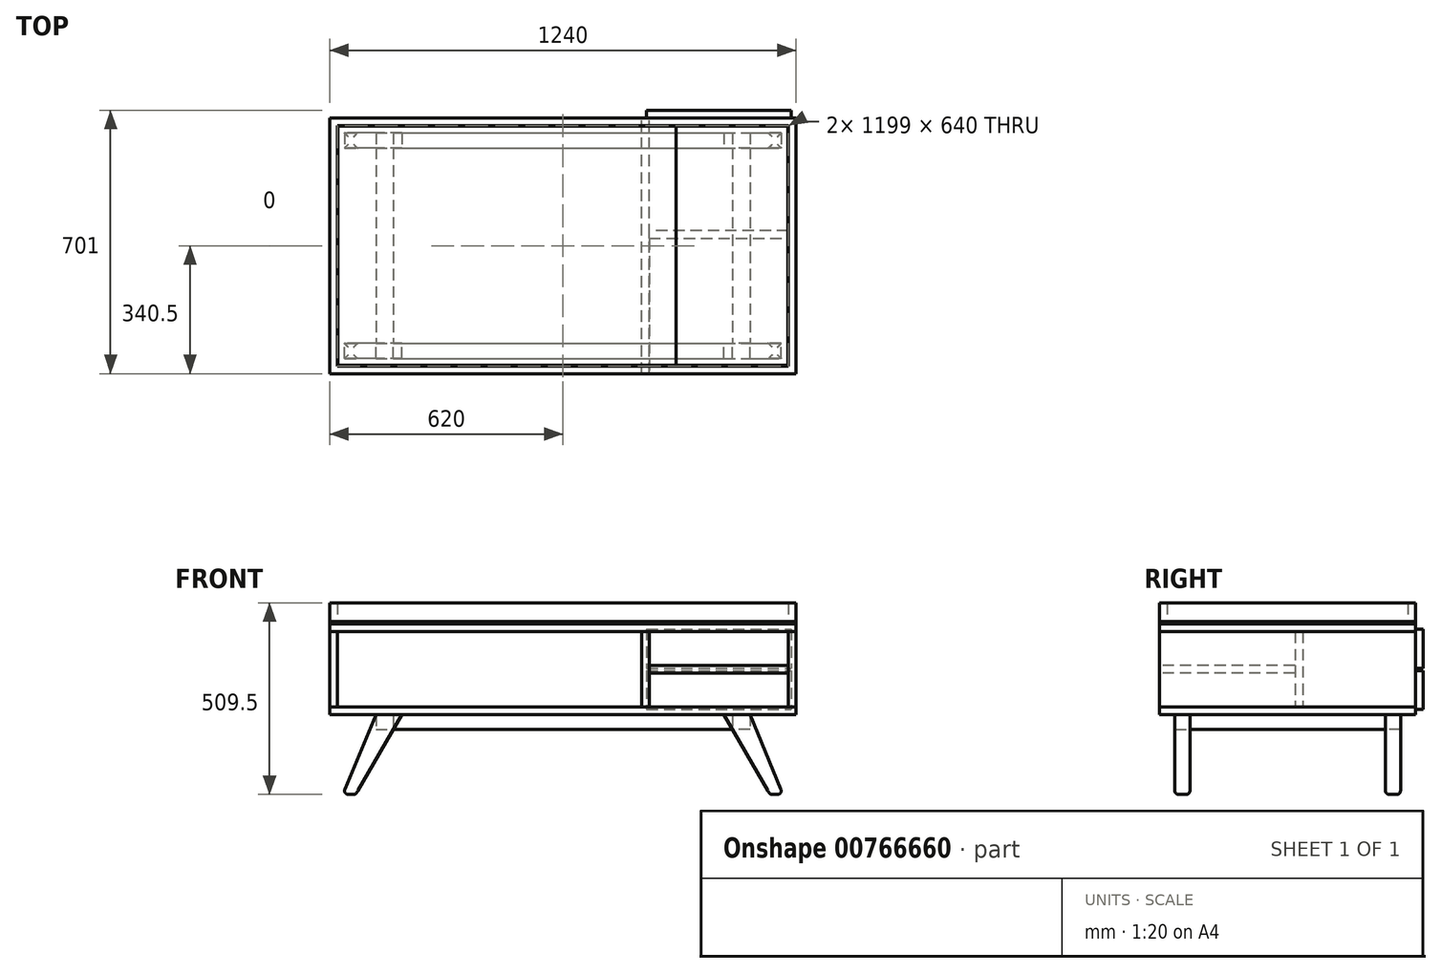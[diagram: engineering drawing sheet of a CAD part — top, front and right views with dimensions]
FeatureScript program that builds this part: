
annotation { "Feature Type Name" : "Feature", "Feature Type Description" : "" }
export const myFeature = defineFeature(function(context is Context, id is Id, definition is map)
    precondition{}
    {
        {
            var Q0;
            Q0=qCreatedBy(makeId("Front.planeOp"),FACE);
            var sketch = newSketch(context, id + "F0", { "sketchPlane" : qUnion([Q0])});
            skLineSegment(sketch, "E0.bottom", {"start": v(-620, 0) * mm, "end": v(620, 0) * mm});
            skLineSegment(sketch, "E0.top", {"start": v(-620, -241) * mm, "end": v(620, -241) * mm});
            skLineSegment(sketch, "E1", {"start": v(229.5, -20.5) * mm, "end": v(229.5, -220.5) * mm});
            skLineSegment(sketch, "E2.0", {"start": v(-620, -20.5) * mm, "end": v(620, -20.5) * mm});
            skLineSegment(sketch, "E2.2", {"start": v(-620, -220.5) * mm, "end": v(620, -220.5) * mm});
            skLineSegment(sketch, "E3.trimOffspring", {"start": v(-599.5, -20.5) * mm, "end": v(-599.5, -220.5) * mm});
            skLineSegment(sketch, "E4.trimOffspring", {"start": v(599.5, -20.5) * mm, "end": v(599.5, -220.5) * mm});
            skLineSegment(sketch, "E5.trimOffspring", {"start": v(-620, 0) * mm, "end": v(-620, -241) * mm});
            skLineSegment(sketch, "E6.trimOffspring", {"start": v(620, 0) * mm, "end": v(620, -241) * mm});
            skLineSegment(sketch, "E7", {"start": v(229.5, -120.5) * mm, "end": v(599.5, -120.5) * mm, "construction": true});
            skLineSegment(sketch, "E8", {"start": v(229.5, -110.25) * mm, "end": v(599.5, -110.25) * mm});
            skLineSegment(sketch, "E9", {"start": v(229.5, -130.75) * mm, "end": v(599.5, -130.75) * mm});
            skLineSegment(sketch, "E10.0", {"start": v(209, -20.5) * mm, "end": v(209, -220.5) * mm});
            skPoint(sketch, "E11", {"position": v(0, 0) * mm});
            skSolve(sketch);
        }
        {
            var Q0;
            {var subQ1=sQuery(id+"F0.wireOp",EDGE,"E0.top");Q0=makeQuery(id+"F0.imprint","IMPRINT",FACE,{"disambiguationData":[TD([[makeQuery(id+"F0.imprint","IMPRINT",EDGE,{"derivedFrom":subQ1}),1.0]])]});}
            extrude(context, id + "F1", {"entities" : qUnion([Q0]), "depth" : 681 / 2 * mm, "offsetDistance" : 25 * mm, "hasSecondDirection" : true, "secondDirectionOppositeDirection" : true, "secondDirectionDepth" : 681 / 2 * mm});
        }
        {
            var Q0;
            {var subQ0=sQuery(id+"F0.wireOp",EDGE,"60a11fd1-bdb7-46c1-8277-bfbef1fc92c4.0");Q0=makeQuery(id+"F0.imprint","IMPRINT",FACE,{"disambiguationData":[TD([[makeQuery(id+"F0.imprint","IMPRINT",EDGE,{"derivedFrom":subQ0}),-1.0]])]});}
            var Q1;
            {var subQ0=sQuery(id+"F0.wireOp",EDGE,"E1");Q1=makeQuery(id+"F0.imprint","IMPRINT",FACE,{"disambiguationData":[TD([[makeQuery(id+"F0.imprint","IMPRINT",EDGE,{"derivedFrom":subQ0}),-1.0]])]});}
            var Q2;
            {var subQ3=sQuery(id+"F0.wireOp",EDGE,"60a11fd1-bdb7-46c1-8277-bfbef1fc92c4.2");Q2=makeQuery(id+"F0.imprint","IMPRINT",FACE,{"disambiguationData":[TD([[makeQuery(id+"F0.imprint","IMPRINT",EDGE,{"derivedFrom":subQ3}),1.0]])]});}
            var Q3;
            {var subQ2=sQuery(id+"F0.wireOp",EDGE,"E2.2");var subQ4=sQuery(id+"F0.wireOp",EDGE,"E0.left");var subQ5=makeQuery(id+"F0.imprint","INTERSECT",VERTEX,{"derivedFrom":[subQ4,subQ2]});Q3=makeQuery(id+"F0.imprint","IMPRINT",FACE,{"disambiguationData":[TD([[makeQuery(id+"F0.imprint","IMPRINT",EDGE,{"disambiguationData":[TD([[subQ5,1.0]])],"derivedFrom":subQ4}),1.0]])]});}
            var Q4;
            {var subQ3=sQuery(id+"F0.wireOp",EDGE,"E3.trimOffspring");Q4=makeQuery(id+"F0.imprint","IMPRINT",FACE,{"disambiguationData":[TD([[makeQuery(id+"F0.imprint","IMPRINT",EDGE,{"derivedFrom":subQ3}),-1.0]])]});}
            var Q5;
            {var subQ3=sQuery(id+"F0.wireOp",EDGE,"E4.trimOffspring");Q5=makeQuery(id+"F0.imprint","IMPRINT",FACE,{"disambiguationData":[TD([[makeQuery(id+"F0.imprint","IMPRINT",EDGE,{"derivedFrom":subQ3}),1.0]])]});}
            var Q6;
            Q6=makeQuery(id+"F1.opExtrude","CAP_FACE",FACE,{"disambiguationData":[OSD([sQuery(id+"F0.wireOp",EDGE,"E0.top"),sQuery(id+"F0.wireOp",EDGE,"E0.left"),sQuery(id+"F0.wireOp",EDGE,"E0.right"),sQuery(id+"F0.wireOp",EDGE,"E2.2")])],"isStart":false});
            var Q7;
            Q7=makeQuery(id+"F1.opExtrude","CAP_FACE",FACE,{"disambiguationData":[OSD([sQuery(id+"F0.wireOp",EDGE,"E0.top"),sQuery(id+"F0.wireOp",EDGE,"E0.left"),sQuery(id+"F0.wireOp",EDGE,"E0.right"),sQuery(id+"F0.wireOp",EDGE,"E2.2")])],"isStart":true});
            extrude(context, id + "F2", {"entities" : qUnion([Q0, Q1, Q2, Q3, Q4, Q5]), "endBound" : BoundingType.UP_TO_SURFACE, "depth" : 25 * mm, "endBoundEntityFace" : qUnion([Q6]), "offsetDistance" : 25 * mm, "hasSecondDirection" : true, "secondDirectionBound" : SecondDirectionBoundingType.UP_TO_SURFACE, "secondDirectionOppositeDirection" : true, "secondDirectionDepth" : 25 * mm, "secondDirectionBoundEntityFace" : qUnion([Q7])});
        }
        {
            var Q0;
            {var subQ6=sQuery(id+"F0.wireOp",EDGE,"E0.bottom");Q0=makeQuery(id+"F0.imprint","IMPRINT",FACE,{"disambiguationData":[TD([[makeQuery(id+"F0.imprint","IMPRINT",EDGE,{"derivedFrom":subQ6}),-1.0]])]});}
            var Q1;
            Q1=makeQuery(id+"F1.opExtrude","CAP_FACE",FACE,{"disambiguationData":[OSD([sQuery(id+"F0.wireOp",EDGE,"E0.top"),sQuery(id+"F0.wireOp",EDGE,"E0.left"),sQuery(id+"F0.wireOp",EDGE,"E0.right"),sQuery(id+"F0.wireOp",EDGE,"E2.2")])],"isStart":false});
            var Q2;
            Q2=makeQuery(id+"F1.opExtrude","CAP_FACE",FACE,{"disambiguationData":[OSD([sQuery(id+"F0.wireOp",EDGE,"E0.top"),sQuery(id+"F0.wireOp",EDGE,"E0.left"),sQuery(id+"F0.wireOp",EDGE,"E0.right"),sQuery(id+"F0.wireOp",EDGE,"E2.2")])],"isStart":true});
            extrude(context, id + "F3", {"entities" : qUnion([Q0]), "endBound" : BoundingType.UP_TO_SURFACE, "depth" : 25 * mm, "endBoundEntityFace" : qUnion([Q1]), "offsetDistance" : 25 * mm, "hasSecondDirection" : true, "secondDirectionBound" : SecondDirectionBoundingType.UP_TO_SURFACE, "secondDirectionOppositeDirection" : true, "secondDirectionDepth" : 25 * mm, "secondDirectionBoundEntityFace" : qUnion([Q2])});
        }
        {
            var Q0;
            Q0=qCreatedBy(makeId("Front.planeOp"),FACE);
            cPlane(context, id + "F4", {"entities" : qUnion([Q0]), "cplaneType" : CPlaneType.OFFSET, "offset" : 260 * mm, "width" : 150 * mm, "height" : 150 * mm});
        }
        {
            var Q0;
            Q0=qCreatedBy(id+"F4.planeOp",FACE);
            var sketch = newSketch(context, id + "F5", { "sketchPlane" : qUnion([Q0])});
            skLineSegment(sketch, "E12", {"start": v(-620, -62.26) * mm, "end": v(-620, -556.12) * mm, "construction": true});
            skLineSegment(sketch, "E13", {"start": v(620, -20.15) * mm, "end": v(620, -556.12) * mm, "construction": true});
            skLineSegment(sketch, "E14", {"start": v(-1066.77, -241) * mm, "end": v(893.35, -241) * mm});
            skLineSegment(sketch, "E15", {"start": v(-497.31, -241) * mm, "end": v(-620, -453.5) * mm});
            skLineSegment(sketch, "E16", {"start": v(-620, -453.5) * mm, "end": v(-550.72, -453.5) * mm});
            skLineSegment(sketch, "E17", {"start": v(-428.03, -241) * mm, "end": v(-550.72, -453.5) * mm});
            skLineSegment(sketch, "E18.MirrorCS", {"start": v(620, -453.5) * mm, "end": v(550.72, -453.5) * mm});
            skLineSegment(sketch, "E19.MirrorCS", {"start": v(497.31, -241) * mm, "end": v(620, -453.5) * mm});
            skLineSegment(sketch, "E20.MirrorCS", {"start": v(428.03, -241) * mm, "end": v(550.72, -453.5) * mm});
            skLineSegment(sketch, "E21", {"start": v(-451.13, -281) * mm, "end": v(451.13, -281) * mm});
            skLineSegment(sketch, "E22", {"start": v(-497.31, -241) * mm, "end": v(-585.36, -453.5) * mm});
            skLineSegment(sketch, "E23", {"start": v(497.31, -241) * mm, "end": v(585.36, -453.5) * mm});
            skSolve(sketch);
        }
        {
            var Q0;
            {var subQ4=sQuery(id+"F5.wireOp",EDGE,"E22");Q0=makeQuery(id+"F5.imprint","IMPRINT",FACE,{"disambiguationData":[TD([[makeQuery(id+"F5.imprint","IMPRINT",EDGE,{"derivedFrom":subQ4}),1.0]])]});}
            var Q1;
            {var subQ4=sQuery(id+"F5.wireOp",EDGE,"E23");Q1=makeQuery(id+"F5.imprint","IMPRINT",FACE,{"disambiguationData":[TD([[makeQuery(id+"F5.imprint","IMPRINT",EDGE,{"derivedFrom":subQ4}),-1.0]])]});}
            extrude(context, id + "F6", {"entities" : qUnion([Q0, Q1]), "depth" : 40 * mm, "offsetDistance" : 25 * mm});
        }
        {
            var Q0;
            Q0=makeQuery(id+"F6.opExtrude","CAP_EDGE",EDGE,{"disambiguationData":[OSD([sQuery(id+"F5.wireOp",EDGE,"E16")])],"isStart":false});
            var Q1;
            Q1=makeQuery(id+"F6.opExtrude","SWEPT_EDGE",EDGE,{"disambiguationData":[OSD([sQuery(id+"F5.wireOp",EDGE,"E16"),sQuery(id+"F5.wireOp",EDGE,"E17")])]});
            var Q2;
            Q2=makeQuery(id+"F6.opExtrude","CAP_EDGE",EDGE,{"disambiguationData":[OSD([sQuery(id+"F5.wireOp",EDGE,"E16")])],"isStart":true});
            var Q3;
            Q3=makeQuery(id+"F6.opExtrude","SWEPT_EDGE",EDGE,{"disambiguationData":[OSD([sQuery(id+"F5.wireOp",EDGE,"E15"),sQuery(id+"F5.wireOp",EDGE,"E16")])]});
            var Q4;
            Q4=makeQuery(id+"F6.opExtrude","CAP_EDGE",EDGE,{"disambiguationData":[OSD([sQuery(id+"F5.wireOp",EDGE,"E18.MirrorCS")])],"isStart":false});
            var Q5;
            Q5=makeQuery(id+"F6.opExtrude","SWEPT_EDGE",EDGE,{"disambiguationData":[OSD([sQuery(id+"F5.wireOp",EDGE,"E18.MirrorCS"),sQuery(id+"F5.wireOp",EDGE,"E20.MirrorCS")])]});
            var Q6;
            Q6=makeQuery(id+"F6.opExtrude","CAP_EDGE",EDGE,{"disambiguationData":[OSD([sQuery(id+"F5.wireOp",EDGE,"E18.MirrorCS")])],"isStart":true});
            var Q7;
            Q7=makeQuery(id+"F6.opExtrude","SWEPT_EDGE",EDGE,{"disambiguationData":[OSD([sQuery(id+"F5.wireOp",EDGE,"E18.MirrorCS"),sQuery(id+"F5.wireOp",EDGE,"E19.MirrorCS")])]});
            fillet(context, id + "F7", {"entities" : qUnion([Q0, Q1, Q2, Q3, Q4, Q5, Q6, Q7]), "tangentPropagation" : true, "radius" : 10 * mm, "defaultsChanged" : true, "vertexSettings" : [], "allowEdgeOverflow" : false});
        }
        {
            var Q0;
            {var subQ5=sQuery(id+"F5.wireOp",EDGE,"E21");Q0=makeQuery(id+"F5.imprint","IMPRINT",FACE,{"disambiguationData":[TD([[makeQuery(id+"F5.imprint","IMPRINT",EDGE,{"derivedFrom":subQ5}),1.0]])]});}
            extrude(context, id + "F8", {"entities" : qUnion([Q0]), "depth" : 40 * mm, "offsetDistance" : 25 * mm});
        }
        {
            var Q0;
            Q0=makeQuery(id+"F6.opExtrude","SWEPT_BODY",BODY,{"disambiguationData":[OSD([sQuery(id+"F5.wireOp",EDGE,"E14"),sQuery(id+"F5.wireOp",EDGE,"E15"),sQuery(id+"F5.wireOp",EDGE,"E16"),sQuery(id+"F5.wireOp",EDGE,"E17")])]});
            var Q1;
            Q1=makeQuery(id+"F6.opExtrude","SWEPT_BODY",BODY,{"disambiguationData":[OSD([sQuery(id+"F5.wireOp",EDGE,"E14"),sQuery(id+"F5.wireOp",EDGE,"E18.MirrorCS"),sQuery(id+"F5.wireOp",EDGE,"E19.MirrorCS"),sQuery(id+"F5.wireOp",EDGE,"E20.MirrorCS")])]});
            var Q2;
            Q2=makeQuery(id+"F8.opExtrude","SWEPT_BODY",BODY,{"disambiguationData":[OSD([sQuery(id+"F5.wireOp",EDGE,"E14"),sQuery(id+"F5.wireOp",EDGE,"E17"),sQuery(id+"F5.wireOp",EDGE,"E20.MirrorCS"),sQuery(id+"F5.wireOp",EDGE,"E21")])]});
            var Q3;
            Q3=qCreatedBy(makeId("Front.planeOp"),FACE);
            mirror(context, id + "F9", {"entities" : qUnion([Q0, Q1, Q2]), "mirrorPlane" : qUnion([Q3])});
        }
        {
            var Q0;
            {var subQ5=sQuery(id+"F5.wireOp",EDGE,"E18.MirrorCS");Q0=makeQuery(id+"F5.imprint","IMPRINT",FACE,{"disambiguationData":[TD([[makeQuery(id+"F5.imprint","IMPRINT",EDGE,{"derivedFrom":subQ5}),-1.0]])]});}
            var sketch = newSketch(context, id + "F10", { "sketchPlane" : qUnion([Q0])});
            skPoint(sketch, "E24.0", {"position": v(497.31, -241) * mm});
            skPoint(sketch, "E25.0", {"position": v(451.13, -281) * mm});
            skLineSegment(sketch, "E26.bottom", {"start": v(497.31, -241) * mm, "end": v(451.13, -241) * mm});
            skLineSegment(sketch, "E26.top", {"start": v(497.31, -281) * mm, "end": v(451.13, -281) * mm});
            skLineSegment(sketch, "E26.left", {"start": v(497.31, -241) * mm, "end": v(497.31, -281) * mm});
            skLineSegment(sketch, "E26.right", {"start": v(451.13, -241) * mm, "end": v(451.13, -281) * mm});
            skLineSegment(sketch, "E27.MirrorCS", {"start": v(-497.31, -241) * mm, "end": v(-451.13, -241) * mm});
            skLineSegment(sketch, "E28.MirrorCS", {"start": v(-451.13, -241) * mm, "end": v(-451.13, -281) * mm});
            skLineSegment(sketch, "E29.MirrorCS", {"start": v(-497.31, -241) * mm, "end": v(-497.31, -281) * mm});
            skLineSegment(sketch, "E30.MirrorCS", {"start": v(-497.31, -281) * mm, "end": v(-451.13, -281) * mm});
            skSolve(sketch);
        }
        {
            var Q0;
            Q0=qSketchRegion(id+"F10",true);
            extrude(context, id + "F11", {"entities" : qUnion([Q0]), "endBound" : BoundingType.UP_TO_NEXT, "oppositeDirection" : true, "depth" : 25 * mm, "offsetDistance" : 25 * mm});
        }
        {
            var Q0;
            Q0=makeQuery(id+"F2.opExtrude","CAP_FACE",FACE,{"disambiguationData":[OSD([sQuery(id+"F0.wireOp",EDGE,"E1"),sQuery(id+"F0.wireOp",EDGE,"E2.0"),sQuery(id+"F0.wireOp",EDGE,"E2.2"),sQuery(id+"F0.wireOp",EDGE,"ae8f2980-7300-4422-b546-210f4e41f4ac.trimOffspring"),sQuery(id+"F0.wireOp",EDGE,"E4.trimOffspring"),sQuery(id+"F0.wireOp",EDGE,"E6.trimOffspring"),sQuery(id+"F0.wireOp",EDGE,"E8"),sQuery(id+"F0.wireOp",EDGE,"E9")])],"isStart":true});
            var sketch = newSketch(context, id + "F12", { "sketchPlane" : qUnion([Q0])});
            skPoint(sketch, "E31.orphan", {"position": v(620, -20.5) * mm});
            skPoint(sketch, "E32.orphan", {"position": v(620, -220.5) * mm});
            skLineSegment(sketch, "E33.0", {"start": v(-229.5, -20.5) * mm, "end": v(-599.5, -20.5) * mm, "construction": true});
            skLineSegment(sketch, "E34.0", {"start": v(-599.5, -20.5) * mm, "end": v(-599.5, -110.25) * mm, "construction": true});
            skLineSegment(sketch, "E35.0", {"start": v(-229.5, -220.5) * mm, "end": v(-599.5, -220.5) * mm, "construction": true});
            skLineSegment(sketch, "E36.0", {"start": v(-229.5, -20.5) * mm, "end": v(-229.5, -110.25) * mm, "construction": true});
            skLineSegment(sketch, "E37.0", {"start": v(-229.5, -110.25) * mm, "end": v(-599.5, -110.25) * mm, "construction": true});
            skLineSegment(sketch, "E38.0", {"start": v(-229.5, -130.75) * mm, "end": v(-599.5, -130.75) * mm, "construction": true});
            skLineSegment(sketch, "E39.trimOffspring", {"start": v(-599.5, -130.75) * mm, "end": v(-599.5, -220.5) * mm, "construction": true});
            skLineSegment(sketch, "E40.trimOffspring", {"start": v(-229.5, -130.75) * mm, "end": v(-229.5, -220.5) * mm, "construction": true});
            skPoint(sketch, "E41.orphan", {"position": v(-620, -220.5) * mm});
            skPoint(sketch, "E42.orphan", {"position": v(-620, -20.5) * mm});
            skLineSegment(sketch, "E43.0", {"start": v(-222.5, -13.5) * mm, "end": v(-606.5, -13.5) * mm});
            skLineSegment(sketch, "E43.1", {"start": v(-222.5, -13.5) * mm, "end": v(-222.5, -117.25) * mm});
            skLineSegment(sketch, "E43.2", {"start": v(-222.5, -117.25) * mm, "end": v(-606.5, -117.25) * mm});
            skLineSegment(sketch, "E43.3", {"start": v(-606.5, -13.5) * mm, "end": v(-606.5, -117.25) * mm});
            skLineSegment(sketch, "E44.0", {"start": v(-222.5, -123.75) * mm, "end": v(-606.5, -123.75) * mm});
            skLineSegment(sketch, "E44.1", {"start": v(-222.5, -123.75) * mm, "end": v(-222.5, -227.5) * mm});
            skLineSegment(sketch, "E44.2", {"start": v(-222.5, -227.5) * mm, "end": v(-606.5, -227.5) * mm});
            skLineSegment(sketch, "E44.3", {"start": v(-606.5, -123.75) * mm, "end": v(-606.5, -227.5) * mm});
            skSolve(sketch);
        }
        {
            var Q0;
            {var subQ0=sQuery(id+"F12.wireOp",EDGE,"E43.3");var subQ1=sQuery(id+"F12.wireOp",EDGE,"E43.2");var subQ2=makeQuery(id+"F12.imprint","INTERSECT",VERTEX,{"derivedFrom":[subQ1,subQ0]});Q0=makeQuery(id+"F12.imprint","IMPRINT",FACE,{"disambiguationData":[TD([[makeQuery(id+"F12.imprint","IMPRINT",EDGE,{"disambiguationData":[TD([[subQ2,1.0]])],"derivedFrom":subQ1}),-1.0]])]});}
            var Q1;
            {var subQ1=sQuery(id+"F12.wireOp",EDGE,"E43.0");Q1=makeQuery(id+"F12.imprint","IMPRINT",FACE,{"disambiguationData":[TD([[makeQuery(id+"F12.imprint","IMPRINT",EDGE,{"derivedFrom":subQ1}),1.0]])]});}
            var Q2;
            {var subQ0=sQuery(id+"F12.wireOp",EDGE,"E44.3");var subQ1=sQuery(id+"F12.wireOp",EDGE,"E44.0");var subQ2=makeQuery(id+"F12.imprint","INTERSECT",VERTEX,{"derivedFrom":[subQ1,subQ0]});Q2=makeQuery(id+"F12.imprint","IMPRINT",FACE,{"disambiguationData":[TD([[makeQuery(id+"F12.imprint","IMPRINT",EDGE,{"disambiguationData":[TD([[subQ2,1.0]])],"derivedFrom":subQ1}),1.0]])]});}
            var Q3;
            {var subQ1=sQuery(id+"F12.wireOp",EDGE,"E44.1");Q3=makeQuery(id+"F12.imprint","IMPRINT",FACE,{"disambiguationData":[TD([[makeQuery(id+"F12.imprint","IMPRINT",EDGE,{"derivedFrom":subQ1}),-1.0]])]});}
            extrude(context, id + "F13", {"entities" : qUnion([Q0, Q1, Q2, Q3]), "depth" : 20 * mm, "offsetDistance" : 25 * mm});
        }
        {
            var Q0;
            Q0=makeQuery(id+"F3.opExtrude","SWEPT_FACE",FACE,{"disambiguationData":[OSD([sQuery(id+"F0.wireOp",EDGE,"E0.bottom")])]});
            var sketch = newSketch(context, id + "F14", { "sketchPlane" : qUnion([Q0])});
            skLineSegment(sketch, "E45.0", {"start": v(-620, -340.5) * mm, "end": v(-620, 340.5) * mm});
            skLineSegment(sketch, "E45.1", {"start": v(-620, 340.5) * mm, "end": v(620, 340.5) * mm});
            skLineSegment(sketch, "E45.2", {"start": v(620, -340.5) * mm, "end": v(620, 340.5) * mm});
            skLineSegment(sketch, "E45.3", {"start": v(-620, -340.5) * mm, "end": v(620, -340.5) * mm});
            skLineSegment(sketch, "E46.0", {"start": v(-599.5, 320) * mm, "end": v(-599.5, -320) * mm});
            skLineSegment(sketch, "E46.1", {"start": v(599.5, 320) * mm, "end": v(-599.5, 320) * mm});
            skLineSegment(sketch, "E46.2", {"start": v(599.5, -320) * mm, "end": v(599.5, 320) * mm});
            skLineSegment(sketch, "E46.3", {"start": v(-599.5, -320) * mm, "end": v(599.5, -320) * mm});
            skLineSegment(sketch, "E47.0", {"start": v(-615, 335.5) * mm, "end": v(-615, -335.5) * mm});
            skLineSegment(sketch, "E47.1", {"start": v(615, 335.5) * mm, "end": v(-615, 335.5) * mm});
            skLineSegment(sketch, "E47.2", {"start": v(615, -335.5) * mm, "end": v(615, 335.5) * mm});
            skLineSegment(sketch, "E47.3", {"start": v(-615, -335.5) * mm, "end": v(615, -335.5) * mm});
            skSolve(sketch);
        }
        {
            var Q0;
            Q0=makeQuery(id+"F14.imprint","IMPRINT",FACE,{"disambiguationData":[TD([[makeQuery(id+"F14.imprint","IMPRINT",EDGE,{"derivedFrom":sQuery(id+"F14.wireOp",EDGE,"E46.0")}),-1.0]])]});
            var Q1;
            Q1=makeQuery(id+"F14.imprint","IMPRINT",FACE,{"disambiguationData":[TD([[makeQuery(id+"F14.imprint","IMPRINT",EDGE,{"derivedFrom":sQuery(id+"F14.wireOp",EDGE,"E45.0")}),-1.0]])]});
            extrude(context, id + "F15", {"entities" : qUnion([Q0, Q1]), "depth" : 6 * mm, "offsetDistance" : 25 * mm});
        }
        {
            var Q0;
            Q0=makeQuery(id+"F3.opExtrude","SWEPT_FACE",FACE,{"disambiguationData":[OSD([sQuery(id+"F0.wireOp",EDGE,"E0.bottom")])]});
            var sketch = newSketch(context, id + "F16", { "sketchPlane" : qUnion([Q0])});
            skLineSegment(sketch, "E48.0", {"start": v(599.5, 320) * mm, "end": v(-599.5, 320) * mm});
            skLineSegment(sketch, "E48.1", {"start": v(-599.5, 320) * mm, "end": v(-599.5, -320) * mm});
            skLineSegment(sketch, "E48.2", {"start": v(-599.5, -320) * mm, "end": v(599.5, -320) * mm});
            skLineSegment(sketch, "E48.3", {"start": v(599.5, -320) * mm, "end": v(599.5, 320) * mm});
            skLineSegment(sketch, "E49", {"start": v(300.5, 320) * mm, "end": v(300.5, -320) * mm});
            skLineSegment(sketch, "E50.0", {"start": v(598, 318.5) * mm, "end": v(-598, 318.5) * mm});
            skLineSegment(sketch, "E50.1", {"start": v(598, -318.5) * mm, "end": v(598, 318.5) * mm});
            skLineSegment(sketch, "E50.2", {"start": v(-598, -318.5) * mm, "end": v(598, -318.5) * mm});
            skLineSegment(sketch, "E50.3", {"start": v(-598, 318.5) * mm, "end": v(-598, -318.5) * mm});
            skSolve(sketch);
        }
        {
            var Q0;
            {var subQ5=sQuery(id+"F16.wireOp",EDGE,"E50.3");Q0=makeQuery(id+"F16.imprint","IMPRINT",FACE,{"disambiguationData":[TD([[makeQuery(id+"F16.imprint","IMPRINT",EDGE,{"derivedFrom":subQ5}),1.0]])]});}
            extrude(context, id + "F17", {"entities" : qUnion([Q0]), "depth" : 3 * mm, "offsetDistance" : 25 * mm});
        }
        {
            var Q0;
            {var subQ5=sQuery(id+"F16.wireOp",EDGE,"E50.1");Q0=makeQuery(id+"F16.imprint","IMPRINT",FACE,{"disambiguationData":[TD([[makeQuery(id+"F16.imprint","IMPRINT",EDGE,{"derivedFrom":subQ5}),1.0]])]});}
            var Q1;
            Q1=makeQuery(id+"F17.opExtrude","CAP_FACE",FACE,{"disambiguationData":[OSD([sQuery(id+"F16.wireOp",EDGE,"E48.0"),sQuery(id+"F16.wireOp",EDGE,"E48.1"),sQuery(id+"F16.wireOp",EDGE,"E48.2"),sQuery(id+"F16.wireOp",EDGE,"E49")])],"isStart":false});
            extrude(context, id + "F18", {"entities" : qUnion([Q0]), "endBound" : BoundingType.UP_TO_SURFACE, "depth" : 25 * mm, "endBoundEntityFace" : qUnion([Q1]), "offsetDistance" : 25 * mm});
        }
        {
            var Q0;
            Q0=makeQuery(id+"F15.opExtrude","CAP_FACE",FACE,{"disambiguationData":[OSD([sQuery(id+"F14.wireOp",EDGE,"E45.0"),sQuery(id+"F14.wireOp",EDGE,"E45.1"),sQuery(id+"F14.wireOp",EDGE,"E45.2"),sQuery(id+"F14.wireOp",EDGE,"E45.3"),sQuery(id+"F14.wireOp",EDGE,"E46.0"),sQuery(id+"F14.wireOp",EDGE,"E46.1"),sQuery(id+"F14.wireOp",EDGE,"E46.2"),sQuery(id+"F14.wireOp",EDGE,"E46.3")])],"isStart":false});
            extrude(context, id + "F19", {"entities" : qUnion([Q0]), "depth" : 50 * mm, "offsetDistance" : 25 * mm});
        }
        {
            var Q0;
            Q0=makeQuery(id+"F19.opExtrude","CAP_FACE",FACE,{"disambiguationData":[OSD([sQuery(id+"F14.wireOp",EDGE,"E45.0"),sQuery(id+"F14.wireOp",EDGE,"E45.1"),sQuery(id+"F14.wireOp",EDGE,"E45.2"),sQuery(id+"F14.wireOp",EDGE,"E45.3"),sQuery(id+"F14.wireOp",EDGE,"E46.0"),sQuery(id+"F14.wireOp",EDGE,"E46.1"),sQuery(id+"F14.wireOp",EDGE,"E46.2"),sQuery(id+"F14.wireOp",EDGE,"E46.3")])],"isStart":false});
            var sketch = newSketch(context, id + "F20", { "sketchPlane" : qUnion([Q0])});
            skLineSegment(sketch, "E51.0", {"start": v(-620, 340.5) * mm, "end": v(620, 340.5) * mm});
            skLineSegment(sketch, "E52.0", {"start": v(-620, -340.5) * mm, "end": v(-620, 340.5) * mm});
            skLineSegment(sketch, "E53.0", {"start": v(-620, -340.5) * mm, "end": v(620, -340.5) * mm});
            skLineSegment(sketch, "E54.0", {"start": v(620, -340.5) * mm, "end": v(620, 340.5) * mm});
            skSolve(sketch);
        }
        {
            var Q0;
            Q0=makeQuery(id+"F2.opExtrude","SWEPT_FACE",FACE,{"disambiguationData":[OSD([sQuery(id+"F0.wireOp",EDGE,"E1")])]});
            var sketch = newSketch(context, id + "F21", { "sketchPlane" : qUnion([Q0])});
            skLineSegment(sketch, "E55.0", {"start": v(-340.5, -20.5) * mm, "end": v(-340.5, -220.5) * mm, "construction": true});
            skLineSegment(sketch, "E56.0", {"start": v(340.5, -20.5) * mm, "end": v(340.5, -220.5) * mm, "construction": true});
            skLineSegment(sketch, "E57.2", {"start": v(19.5, -20.5) * mm, "end": v(40, -20.5) * mm});
            skLineSegment(sketch, "E57.3", {"start": v(19.5, -220.5) * mm, "end": v(40, -220.5) * mm});
            skLineSegment(sketch, "E58", {"start": v(19.5, -20.5) * mm, "end": v(19.5, -130.75) * mm});
            skLineSegment(sketch, "E59", {"start": v(40, -20.5) * mm, "end": v(40, -130.75) * mm});
            skLineSegment(sketch, "E60", {"start": v(40, -220.5) * mm, "end": v(19.5, -220.5) * mm});
            skPoint(sketch, "E61.orphan", {"position": v(-340.5, -220.5) * mm});
            skPoint(sketch, "E62.orphan", {"position": v(340.5, -220.5) * mm});
            skPoint(sketch, "E63.orphan", {"position": v(340.5, -110.25) * mm});
            skPoint(sketch, "E64.orphan", {"position": v(340.5, -130.75) * mm});
            skPoint(sketch, "E65.orphan", {"position": v(-340.5, -110.25) * mm});
            skPoint(sketch, "E66.orphan", {"position": v(-340.5, -130.75) * mm});
            skLineSegment(sketch, "E67.trimOffspring", {"start": v(40, -130.75) * mm, "end": v(40, -220.5) * mm});
            skLineSegment(sketch, "E68.trimOffspring", {"start": v(19.5, -130.75) * mm, "end": v(19.5, -220.5) * mm});
            skSolve(sketch);
        }
        {
            var Q0;
            Q0=makeQuery(id+"F21.imprint","IMPRINT",FACE,{"disambiguationData":[TD([[makeQuery(id+"F21.imprint","IMPRINT",EDGE,{"derivedFrom":sQuery(id+"F21.wireOp",EDGE,"E58")}),1.0]])]});
            extrude(context, id + "F22", {"entities" : qUnion([Q0]), "endBound" : BoundingType.UP_TO_NEXT, "depth" : 25 * mm, "offsetDistance" : 25 * mm});
        }
        {
            var Q0;
            {var subQ2=sQuery(id+"F0.wireOp",EDGE,"E8");Q0=makeQuery(id+"F0.imprint","IMPRINT",FACE,{"disambiguationData":[TD([[makeQuery(id+"F0.imprint","IMPRINT",EDGE,{"derivedFrom":subQ2}),-1.0]])]});}
            var Q1;
            Q1=makeQuery(id+"F2.opExtrude","CAP_FACE",FACE,{"disambiguationData":[OSD([sQuery(id+"F0.wireOp",EDGE,"E1"),sQuery(id+"F0.wireOp",EDGE,"E2.0"),sQuery(id+"F0.wireOp",EDGE,"E2.2"),sQuery(id+"F0.wireOp",EDGE,"E10.0")])],"isStart":false});
            extrude(context, id + "F23", {"entities" : qUnion([Q0]), "endBound" : BoundingType.UP_TO_NEXT, "oppositeDirection" : true, "depth" : 25 * mm, "offsetDistance" : 25 * mm, "hasSecondDirection" : true, "secondDirectionBound" : SecondDirectionBoundingType.UP_TO_SURFACE, "secondDirectionOppositeDirection" : false, "secondDirectionDepth" : 25 * mm, "secondDirectionBoundEntityFace" : qUnion([Q1])});
        }
    });
